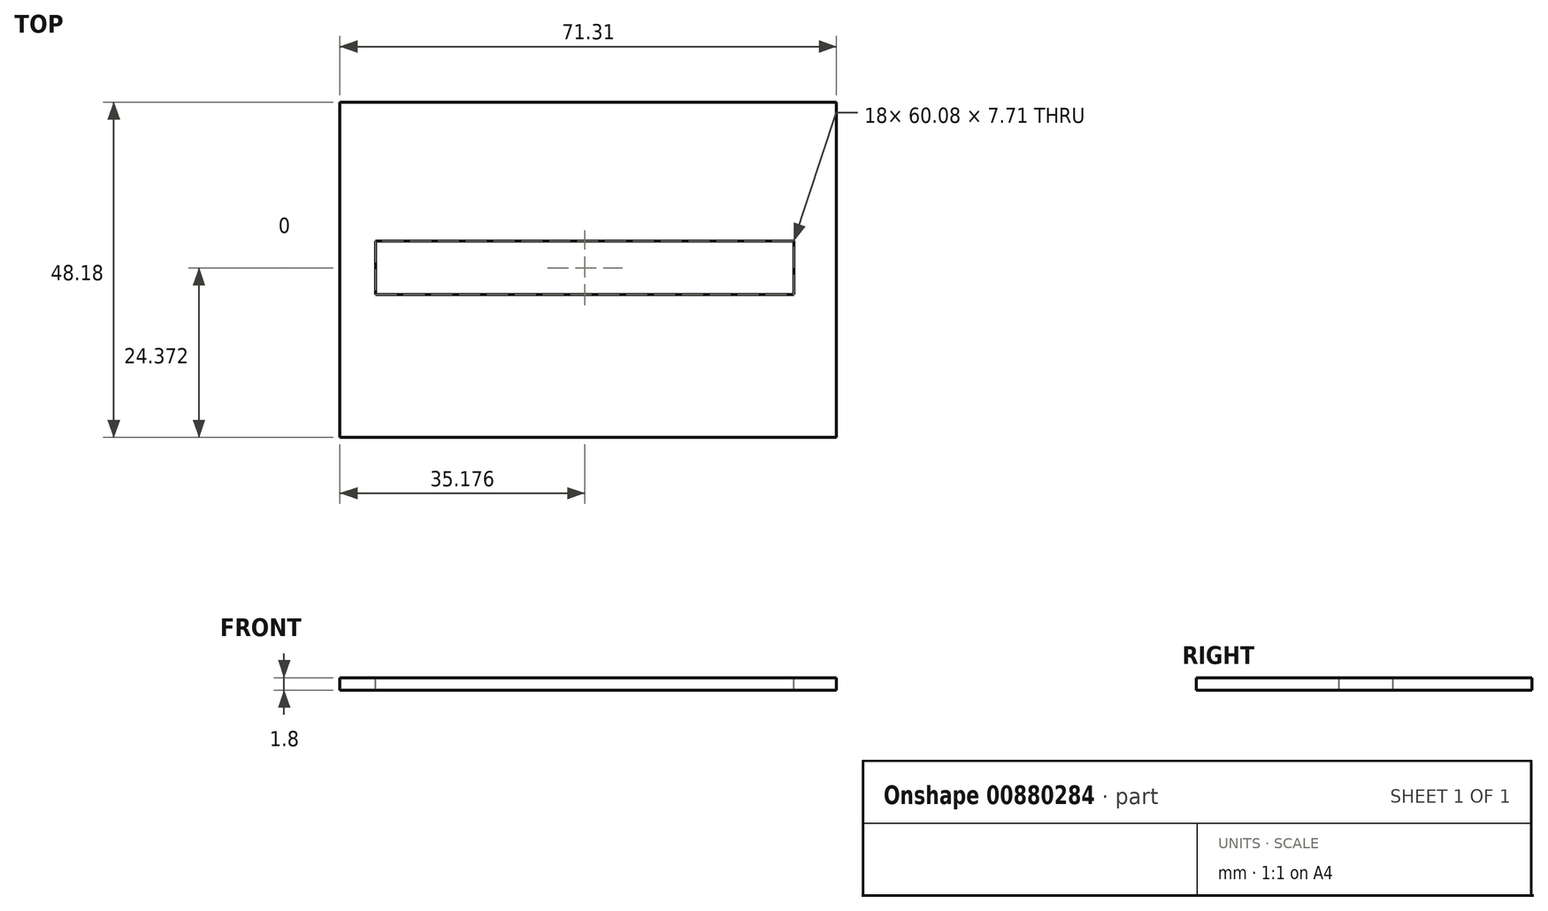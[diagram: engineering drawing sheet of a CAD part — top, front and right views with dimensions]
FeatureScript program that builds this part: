
annotation { "Feature Type Name" : "Feature", "Feature Type Description" : "" }
export const myFeature = defineFeature(function(context is Context, id is Id, definition is map)
    precondition{}
    {
        {
            var Q0;
            Q0=qCreatedBy(makeId("Top.planeOp"),FACE);
            var sketch = newSketch(context, id + "F0", { "sketchPlane" : qUnion([Q0])});
            skLineSegment(sketch, "E0.bottom", {"start": v(-30.73, 12.05) * mm, "end": v(40.58, 12.05) * mm});
            skLineSegment(sketch, "E0.top", {"start": v(-30.73, -36.13) * mm, "end": v(40.58, -36.13) * mm});
            skLineSegment(sketch, "E0.left", {"start": v(-30.73, 12.05) * mm, "end": v(-30.73, -36.13) * mm});
            skLineSegment(sketch, "E0.right", {"start": v(40.58, 12.05) * mm, "end": v(40.58, -36.13) * mm});
            skSolve(sketch);
        }
        {
            var Q0;
            Q0=makeQuery(id+"F0.imprint","IMPRINT",FACE,{"disambiguationData":[TD([[makeQuery(id+"F0.imprint","IMPRINT",EDGE,{"derivedFrom":sQuery(id+"F0.wireOp",EDGE,"E0.bottom")}),-1.0]])]});
            extrude(context, id + "F1", {"entities" : qUnion([Q0]), "depth" : 1.8 * mm, "offsetDistance" : 25 * mm});
        }
        {
            var Q0;
            Q0=qCreatedBy(makeId("Top.planeOp"),FACE);
            var sketch = newSketch(context, id + "F2", { "sketchPlane" : qUnion([Q0])});
            skLineSegment(sketch, "E1.bottom", {"start": v(-25.6, -15.61) * mm, "end": v(34.48, -15.61) * mm});
            skLineSegment(sketch, "E1.top", {"start": v(-25.6, -7.9) * mm, "end": v(34.48, -7.9) * mm});
            skLineSegment(sketch, "E1.left", {"start": v(-25.6, -15.61) * mm, "end": v(-25.6, -7.9) * mm});
            skLineSegment(sketch, "E1.right", {"start": v(34.48, -15.61) * mm, "end": v(34.48, -7.9) * mm});
            skSolve(sketch);
        }
        {
            var Q0;
            Q0=makeQuery(id+"F2.imprint","IMPRINT",FACE,{"disambiguationData":[TD([[makeQuery(id+"F2.imprint","IMPRINT",EDGE,{"derivedFrom":sQuery(id+"F2.wireOp",EDGE,"E1.bottom")}),1.0]])]});
            extrude(context, id + "F3", {"entities" : qUnion([Q0]), "operationType" : NewBodyOperationType.REMOVE, "oppositeDirection" : true, "depth" : 25 * mm, "offsetDistance" : 25 * mm, "hasSecondDirection" : true, "secondDirectionOppositeDirection" : false, "secondDirectionDepth" : 25 * mm});
        }
    });
